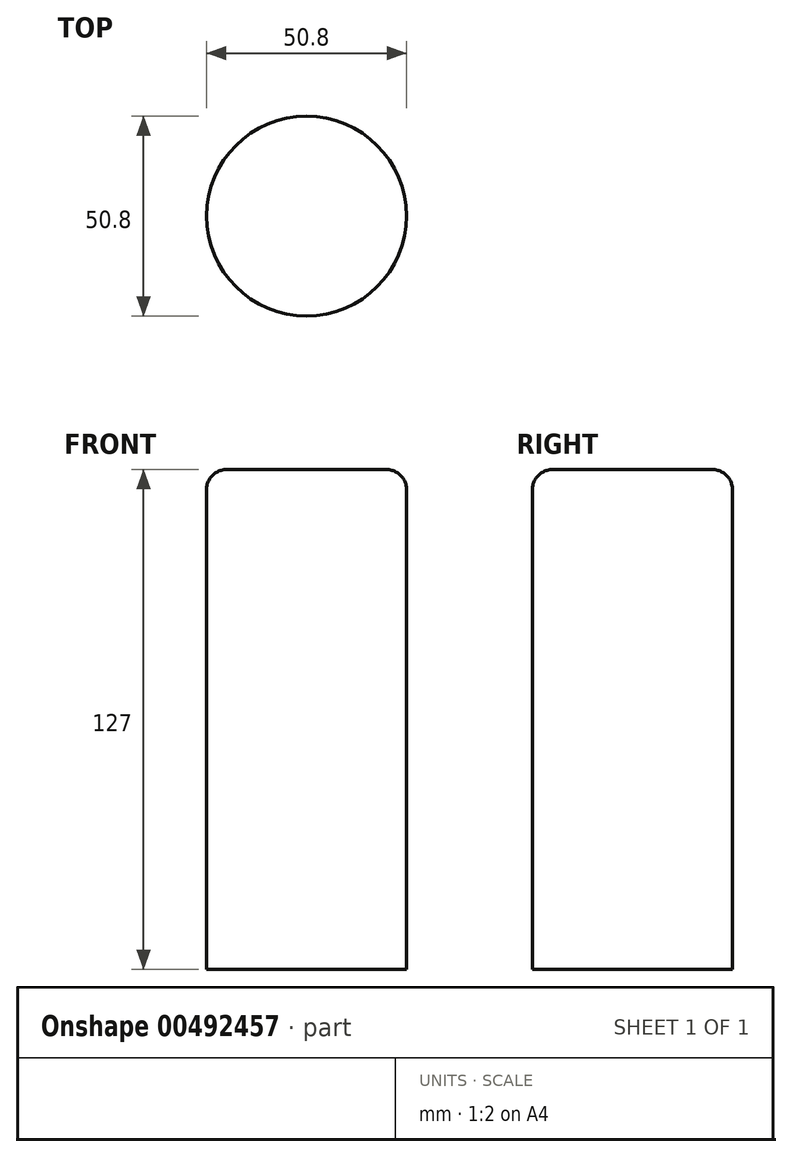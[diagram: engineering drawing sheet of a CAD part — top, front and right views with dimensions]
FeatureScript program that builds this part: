
annotation { "Feature Type Name" : "Feature", "Feature Type Description" : "" }
export const myFeature = defineFeature(function(context is Context, id is Id, definition is map)
    precondition{}
    {
        {
            var Q0;
            Q0=qCreatedBy(makeId("Front.planeOp"),FACE);
            var sketch = newSketch(context, id + "F0", { "sketchPlane" : qUnion([Q0])});
            skLineSegment(sketch, "E0.bottom", {"start": v(0, 0) * mm, "end": v(25.4, 0) * mm});
            skLineSegment(sketch, "E0.top", {"start": v(0, 127) * mm, "end": v(25.4, 127) * mm});
            skLineSegment(sketch, "E0.left", {"start": v(0, 0) * mm, "end": v(0, 127) * mm});
            skLineSegment(sketch, "E0.right", {"start": v(25.4, 0) * mm, "end": v(25.4, 127) * mm});
            skSolve(sketch);
        }
        {
            var Q0;
            Q0=makeQuery(id+"F0.imprint","IMPRINT",FACE,{"disambiguationData":[TD([[makeQuery(id+"F0.imprint","IMPRINT",EDGE,{"derivedFrom":sQuery(id+"F0.wireOp",EDGE,"E0.bottom")}),1.0]])]});
            var Q1;
            Q1=sQuery(id+"F0.wireOp",EDGE,"E0.left");
            revolve(context, id + "F1", {"entities" : qUnion([Q0]), "axis" : qUnion([Q1]), "revolveType" : RevolveType.FULL});
        }
        {
            var Q0;
            Q0=makeQuery(id+"F1.opRevolve","SWEPT_EDGE",EDGE,{"disambiguationData":[OSD([sQuery(id+"F0.wireOp",EDGE,"E0.top"),sQuery(id+"F0.wireOp",EDGE,"E0.right")])]});
            var Q1;
            Q1=makeQuery(id+"F1.opRevolve","SWEPT_FACE",FACE,{"disambiguationData":[OSD([sQuery(id+"F0.wireOp",EDGE,"E0.top")])]});
            fillet(context, id + "F2", {"entities" : qUnion([Q0, Q1]), "radius" : 5.08 * mm, "tangentPropagation" : true, "allowEdgeOverflow" : false});
        }
    });
